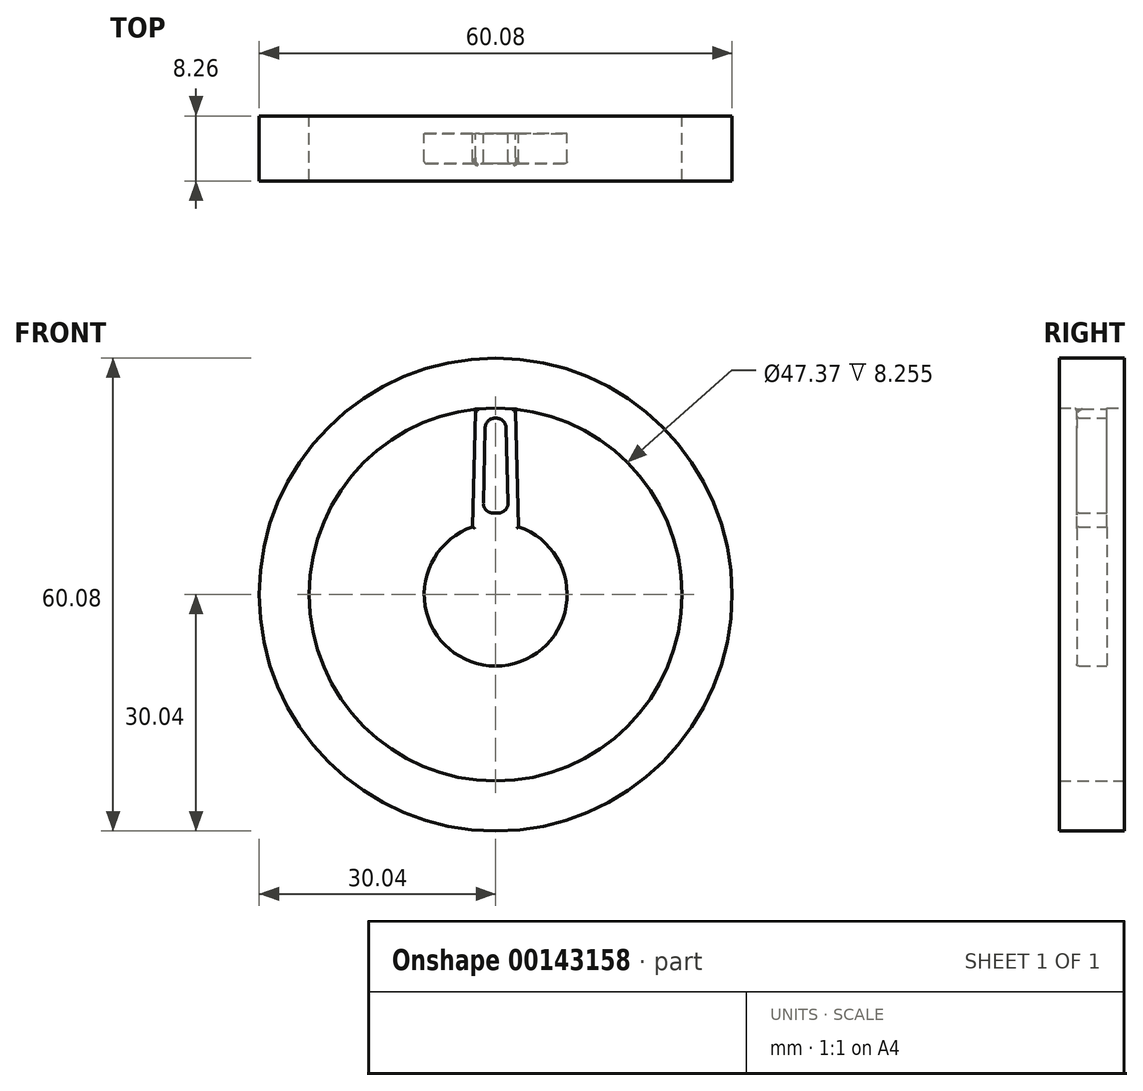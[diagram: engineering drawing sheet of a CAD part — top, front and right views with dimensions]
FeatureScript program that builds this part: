
annotation { "Feature Type Name" : "Feature", "Feature Type Description" : "" }
export const myFeature = defineFeature(function(context is Context, id is Id, definition is map)
    precondition{}
    {
        {
            var Q0;
            Q0=qCreatedBy(makeId("Front.planeOp"),FACE);
            var sketch = newSketch(context, id + "F0", { "sketchPlane" : qUnion([Q0])});
            skCircle(sketch, "E0", {"center": v(0, 0) * mm, "radius": 30.04 * mm});
            skLineSegment(sketch, "E1", {"start": v(0, 0) * mm, "end": v(0, 30.04) * mm, "construction": true});
            skLineSegment(sketch, "E2", {"start": v(-2.92, 8.6) * mm, "end": v(-2.54, 23.55) * mm});
            skLineSegment(sketch, "E3.MirrorCS", {"start": v(2.92, 8.6) * mm, "end": v(2.54, 23.55) * mm});
            skArc(sketch, "E4", {"start": v(2.54, 23.55) * mm, "mid": v(0, 23.69) * mm, "end": v(-2.54, 23.55) * mm});
            skArc(sketch, "E5", {"start": v(-2.54, 23.55) * mm, "mid": v(0, -23.69) * mm, "end": v(2.54, 23.55) * mm});
            skLineSegment(sketch, "E6.0", {"start": v(-1.6, 10.22) * mm, "end": v(-1.3, 22.38) * mm});
            skArc(sketch, "E6.1", {"start": v(1.3, 22.38) * mm, "mid": v(0, 22.42) * mm, "end": v(-1.3, 22.38) * mm});
            skLineSegment(sketch, "E6.2", {"start": v(1.6, 10.22) * mm, "end": v(1.3, 22.38) * mm});
            skArc(sketch, "E7", {"start": v(2.92, 8.6) * mm, "mid": v(0, 9.08) * mm, "end": v(-2.92, 8.6) * mm});
            skArc(sketch, "E8", {"start": v(-2.92, 8.6) * mm, "mid": v(0, -9.08) * mm, "end": v(2.92, 8.6) * mm});
            skArc(sketch, "E9.trimOffspring", {"start": v(1.6, 10.22) * mm, "mid": v(0, 10.35) * mm, "end": v(-1.6, 10.22) * mm});
            skSolve(sketch);
        }
        {
            var Q0;
            Q0=makeQuery(id+"F0.imprint","IMPRINT",FACE,{"disambiguationData":[TD([[makeQuery(id+"F0.imprint","IMPRINT",EDGE,{"derivedFrom":sQuery(id+"F0.wireOp",EDGE,"E0")}),1.0]])]});
            extrude(context, id + "F1", {"entities" : qUnion([Q0]), "depth" : 8.25 * mm, "symmetric" : true});
        }
        {
            var Q0;
            {var subQ0=sQuery(id+"F0.wireOp",EDGE,"E2");Q0=makeQuery(id+"F0.imprint","IMPRINT",FACE,{"disambiguationData":[TD([[makeQuery(id+"F0.imprint","IMPRINT",EDGE,{"derivedFrom":subQ0}),-1.0]])]});}
            var Q1;
            {var subQ0=sQuery(id+"F0.wireOp",EDGE,"03924141-ccc0-40f7-bbcf-2191c8a1f289.1.0");Q1=makeQuery(id+"F0.imprint","IMPRINT",FACE,{"disambiguationData":[TD([[makeQuery(id+"F0.imprint","IMPRINT",EDGE,{"derivedFrom":subQ0}),-1.0]])]});}
            var Q2;
            {var subQ0=sQuery(id+"F0.wireOp",EDGE,"03924141-ccc0-40f7-bbcf-2191c8a1f289.2.0");Q2=makeQuery(id+"F0.imprint","IMPRINT",FACE,{"disambiguationData":[TD([[makeQuery(id+"F0.imprint","IMPRINT",EDGE,{"derivedFrom":subQ0}),-1.0]])]});}
            var Q3;
            {var subQ0=sQuery(id+"F0.wireOp",EDGE,"M8UcVZEs-lOOM-NNK1-Szat-JsytSq5i8szN");var subQ7=makeQuery(id+"F0.imprint","INTERSECT",VERTEX,{"derivedFrom":[subQ0,sQuery(id+"F0.wireOp",EDGE,"E3.MirrorCS")]});Q3=makeQuery(id+"F0.imprint","IMPRINT",FACE,{"disambiguationData":[TD([[makeQuery(id+"F0.imprint","IMPRINT",EDGE,{"disambiguationData":[TD([[subQ7,1.0]])],"derivedFrom":subQ0}),1.0]])]});}
            var Q4;
            {var subQ0=sQuery(id+"F0.wireOp",EDGE,"03924141-ccc0-40f7-bbcf-2191c8a1f289.3.0");Q4=makeQuery(id+"F0.imprint","IMPRINT",FACE,{"disambiguationData":[TD([[makeQuery(id+"F0.imprint","IMPRINT",EDGE,{"derivedFrom":subQ0}),-1.0]])]});}
            var Q5;
            {var subQ0=sQuery(id+"F0.wireOp",EDGE,"03924141-ccc0-40f7-bbcf-2191c8a1f289.4.0");Q5=makeQuery(id+"F0.imprint","IMPRINT",FACE,{"disambiguationData":[TD([[makeQuery(id+"F0.imprint","IMPRINT",EDGE,{"derivedFrom":subQ0}),-1.0]])]});}
            extrude(context, id + "F2", {"entities" : qUnion([Q0, Q1, Q2, Q3, Q4, Q5]), "operationType" : NewBodyOperationType.ADD, "depth" : 3.8 * mm, "symmetric" : true});
        }
        {
            var Q0;
            Q0=makeQuery(id+"F0.imprint","IMPRINT",FACE,{"disambiguationData":[TD([[makeQuery(id+"F0.imprint","IMPRINT",EDGE,{"derivedFrom":sQuery(id+"F0.wireOp",EDGE,"E7")}),1.0]])]});
            extrude(context, id + "F3", {"entities" : qUnion([Q0]), "operationType" : NewBodyOperationType.ADD, "depth" : 3.8 * mm, "symmetric" : true});
        }
        {
            var Q0;
            Q0=makeQuery(id+"F2.opExtrude","SWEPT_EDGE",EDGE,{"disambiguationData":[OSD([sQuery(id+"F0.wireOp",EDGE,"E2"),sQuery(id+"F0.wireOp",EDGE,"E7"),sQuery(id+"F0.wireOp",EDGE,"E8")])]});
            var Q1;
            Q1=makeQuery(id+"F2.opExtrude","SWEPT_EDGE",EDGE,{"disambiguationData":[OSD([sQuery(id+"F0.wireOp",EDGE,"E3.MirrorCS"),sQuery(id+"F0.wireOp",EDGE,"E7"),sQuery(id+"F0.wireOp",EDGE,"E8")])]});
            var Q2;
            Q2=makeQuery(id+"F2.opExtrude","SWEPT_EDGE",EDGE,{"disambiguationData":[OSD([sQuery(id+"F0.wireOp",EDGE,"E6.2"),sQuery(id+"F0.wireOp",EDGE,"E9.trimOffspring")])]});
            var Q3;
            Q3=makeQuery(id+"F2.opExtrude","SWEPT_EDGE",EDGE,{"disambiguationData":[OSD([sQuery(id+"F0.wireOp",EDGE,"E6.0"),sQuery(id+"F0.wireOp",EDGE,"E9.trimOffspring")])]});
            var Q4;
            Q4=makeQuery(id+"F2.opExtrude","SWEPT_EDGE",EDGE,{"disambiguationData":[OSD([sQuery(id+"F0.wireOp",EDGE,"E6.1"),sQuery(id+"F0.wireOp",EDGE,"E6.2")])]});
            var Q5;
            Q5=makeQuery(id+"F2.opExtrude","SWEPT_EDGE",EDGE,{"disambiguationData":[OSD([sQuery(id+"F0.wireOp",EDGE,"E6.0"),sQuery(id+"F0.wireOp",EDGE,"E6.1")])]});
            var Q6;
            Q6=makeQuery(id+"F2.opExtrude","CAP_EDGE",EDGE,{"disambiguationData":[OSD([sQuery(id+"F0.wireOp",EDGE,"E4")])],"isStart":false});
            var Q7;
            Q7=makeQuery(id+"F2.opExtrude","SWEPT_EDGE",EDGE,{"disambiguationData":[OSD([sQuery(id+"F0.wireOp",EDGE,"E3.MirrorCS"),sQuery(id+"F0.wireOp",EDGE,"E4"),sQuery(id+"F0.wireOp",EDGE,"E5")])]});
            var Q8;
            Q8=makeQuery(id+"F2.opExtrude","SWEPT_EDGE",EDGE,{"disambiguationData":[OSD([sQuery(id+"F0.wireOp",EDGE,"E2"),sQuery(id+"F0.wireOp",EDGE,"E4"),sQuery(id+"F0.wireOp",EDGE,"E5")])]});
            fillet(context, id + "F4", {"entities" : qUnion([Q0, Q1, Q2, Q3, Q4, Q5, Q6, Q7, Q8]), "radius" : 1.27 * mm, "tangentPropagation" : true, "allowEdgeOverflow" : false});
        }
        {
            var Q0;
            {var subQ0=sQuery(id+"F0.wireOp",EDGE,"E9.trimOffspring");var subQ1=sQuery(id+"F0.wireOp",EDGE,"E7");var subQ2=sQuery(id+"F0.wireOp",EDGE,"E6.2");var subQ3=sQuery(id+"F0.wireOp",EDGE,"E6.1");var subQ4=sQuery(id+"F0.wireOp",EDGE,"E6.0");var subQ5=sQuery(id+"F0.wireOp",EDGE,"E4");var subQ6=sQuery(id+"F0.wireOp",EDGE,"E3.MirrorCS");var subQ7=sQuery(id+"F0.wireOp",EDGE,"E2");Q0=makeQuery(id+"FUEqxLkX2wMUQ42_1.4.F2.boolean.opBoolean","MERGE",FACE,{"derivedFrom":[makeQuery(id+"FUEqxLkX2wMUQ42_1.3.F2.boolean.opBoolean","MERGE",FACE,{"derivedFrom":[makeQuery(id+"FUEqxLkX2wMUQ42_1.2.F2.boolean.opBoolean","MERGE",FACE,{"derivedFrom":[makeQuery(id+"FUEqxLkX2wMUQ42_1.1.F2.boolean.opBoolean","MERGE",FACE,{"derivedFrom":[makeQuery(id+"F3.boolean.opBoolean","MERGE",FACE,{"derivedFrom":[makeQuery(id+"F2.opExtrude","CAP_FACE",FACE,{"disambiguationData":[OSD([subQ7,subQ6,subQ5,subQ4,subQ3,subQ2,subQ1,subQ0])],"isStart":false}),makeQuery(id+"F3.opExtrude","CAP_FACE",FACE,{"disambiguationData":[OSD([subQ1,sQuery(id+"F0.wireOp",EDGE,"E8")])],"isStart":false})]}),makeQuery(id+"FUEqxLkX2wMUQ42_1.1.F2.opExtrude","CAP_FACE",FACE,{"disambiguationData":[OSD([subQ7,subQ6,subQ5,subQ4,subQ3,subQ2,subQ1,subQ0])],"isStart":false})]}),makeQuery(id+"FUEqxLkX2wMUQ42_1.2.F2.opExtrude","CAP_FACE",FACE,{"disambiguationData":[OSD([subQ7,subQ6,subQ5,subQ4,subQ3,subQ2,subQ1,subQ0])],"isStart":false})]}),makeQuery(id+"FUEqxLkX2wMUQ42_1.3.F2.opExtrude","CAP_FACE",FACE,{"disambiguationData":[OSD([subQ7,subQ6,subQ5,subQ4,subQ3,subQ2,subQ1,subQ0])],"isStart":false})]}),makeQuery(id+"FUEqxLkX2wMUQ42_1.4.F2.opExtrude","CAP_FACE",FACE,{"disambiguationData":[OSD([subQ7,subQ6,subQ5,subQ4,subQ3,subQ2,subQ1,subQ0])],"isStart":false})]});}
            fillet(context, id + "F5", {"entities" : qUnion([Q0]), "radius" : 0.25 * mm, "tangentPropagation" : true, "allowEdgeOverflow" : false});
        }
    });
